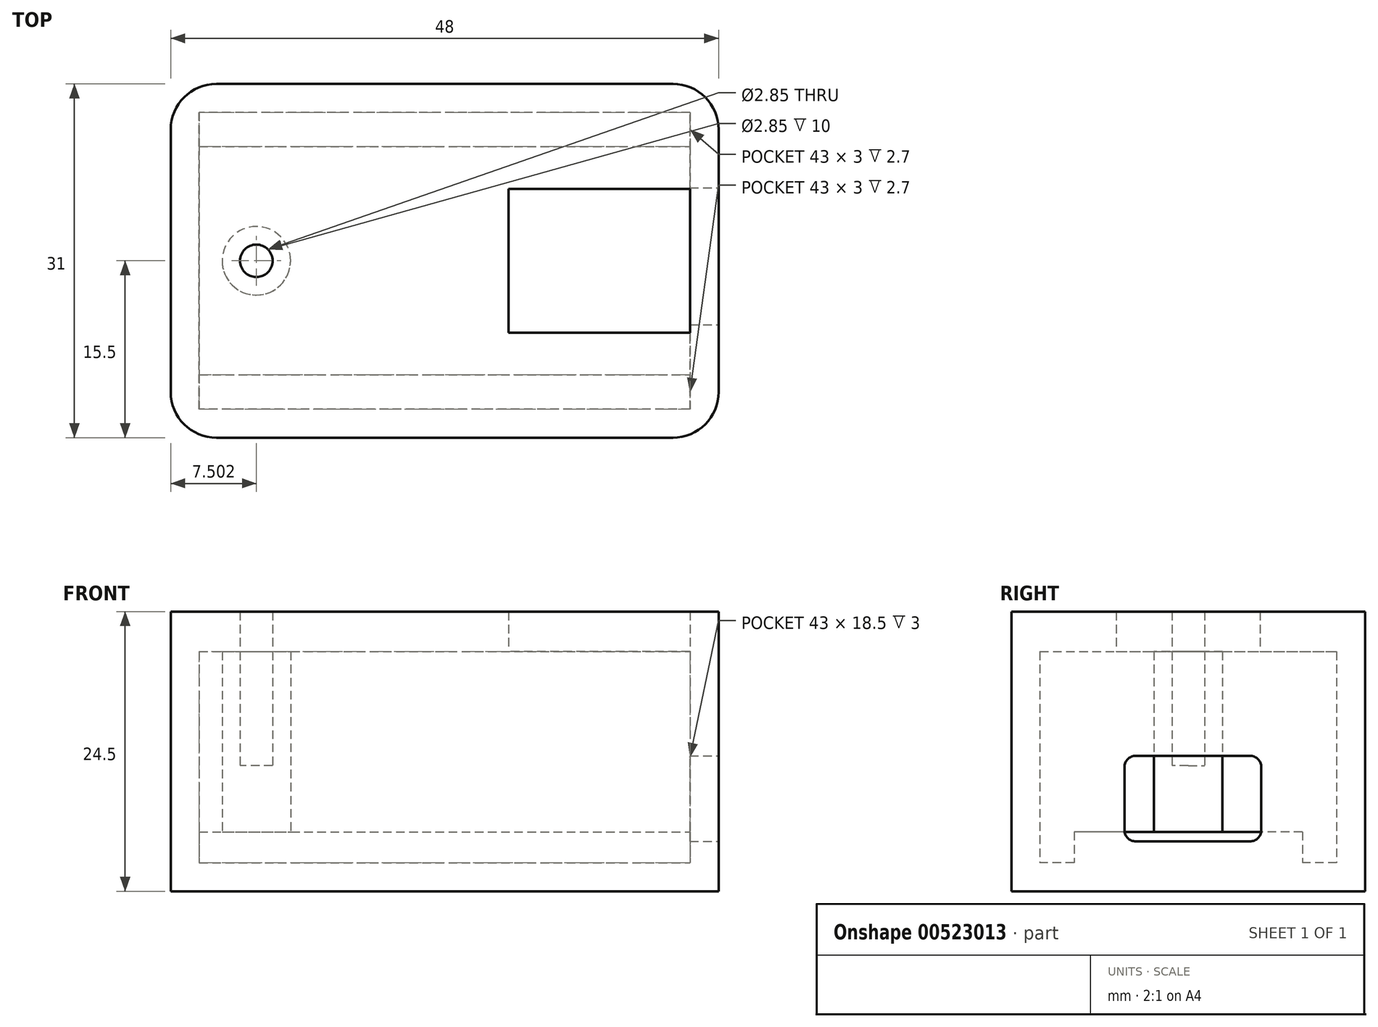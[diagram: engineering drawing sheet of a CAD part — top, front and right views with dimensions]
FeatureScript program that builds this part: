
annotation { "Feature Type Name" : "Feature", "Feature Type Description" : "" }
export const myFeature = defineFeature(function(context is Context, id is Id, definition is map)
    precondition{}
    {
        {
            var Q0;
            Q0=qCreatedBy(makeId("Top.planeOp"),FACE);
            var sketch = newSketch(context, id + "F0", { "sketchPlane" : qUnion([Q0])});
            skLineSegment(sketch, "E0.bottom", {"start": v(24, 15.5) * mm, "end": v(-24, 15.5) * mm});
            skLineSegment(sketch, "E0.top", {"start": v(24, -15.5) * mm, "end": v(-24, -15.5) * mm});
            skLineSegment(sketch, "E0.left", {"start": v(24, 15.5) * mm, "end": v(24, -15.5) * mm});
            skLineSegment(sketch, "E0.right", {"start": v(-24, 15.5) * mm, "end": v(-24, -15.5) * mm});
            skPoint(sketch, "E0.middle", {"position": v(0, 0) * mm});
            skSolve(sketch);
        }
        {
            var Q0;
            Q0=makeQuery(id+"F0.imprint","IMPRINT",FACE,{"disambiguationData":[TD([[makeQuery(id+"F0.imprint","IMPRINT",EDGE,{"derivedFrom":sQuery(id+"F0.wireOp",EDGE,"E0.bottom")}),1.0]])]});
            extrude(context, id + "F1", {"entities" : qUnion([Q0]), "depth" : 22 * mm, "offsetDistance" : 25 * mm});
        }
        {
            var Q0;
            Q0=makeQuery(id+"F1.opExtrude","CAP_FACE",FACE,{"disambiguationData":[OSD([sQuery(id+"F0.wireOp",EDGE,"E0.bottom"),sQuery(id+"F0.wireOp",EDGE,"E0.top"),sQuery(id+"F0.wireOp",EDGE,"E0.left"),sQuery(id+"F0.wireOp",EDGE,"E0.right")])],"isStart":false});
            shell(context, id + "F2", {"entities" : qUnion([Q0]), "thickness" : 2.5 * mm});
        }
        {
            var Q0;
            Q0=makeQuery(id+"F2.opShell","OFFSET_FACE",FACE,{"disambiguationData":[OSD([sQuery(id+"F0.wireOp",EDGE,"E0.bottom"),sQuery(id+"F0.wireOp",EDGE,"E0.top"),sQuery(id+"F0.wireOp",EDGE,"E0.left"),sQuery(id+"F0.wireOp",EDGE,"E0.right")])]});
            var sketch = newSketch(context, id + "F3", { "sketchPlane" : qUnion([Q0])});
            skLineSegment(sketch, "E1.bottom", {"start": v(-21.5, 10) * mm, "end": v(21.5, 10) * mm});
            skLineSegment(sketch, "E1.top", {"start": v(-21.5, -10) * mm, "end": v(21.5, -10) * mm});
            skLineSegment(sketch, "E1.left", {"start": v(-21.5, 10) * mm, "end": v(-21.5, -10) * mm});
            skLineSegment(sketch, "E1.right", {"start": v(21.5, 10) * mm, "end": v(21.5, -10) * mm});
            skPoint(sketch, "E1.middle", {"position": v(0, 0) * mm});
            skSolve(sketch);
        }
        {
            var Q0;
            Q0=makeQuery(id+"F3.imprint","IMPRINT",FACE,{"disambiguationData":[TD([[makeQuery(id+"F3.imprint","IMPRINT",EDGE,{"derivedFrom":sQuery(id+"F3.wireOp",EDGE,"E1.bottom")}),-1.0]])]});
            extrude(context, id + "F4", {"entities" : qUnion([Q0]), "operationType" : NewBodyOperationType.ADD, "depth" : 2.7 * mm, "offsetDistance" : 25 * mm});
        }
        {
            var Q0;
            Q0=makeQuery(id+"F1.opExtrude","CAP_FACE",FACE,{"disambiguationData":[OSD([sQuery(id+"F0.wireOp",EDGE,"E0.bottom"),sQuery(id+"F0.wireOp",EDGE,"E0.top"),sQuery(id+"F0.wireOp",EDGE,"E0.left"),sQuery(id+"F0.wireOp",EDGE,"E0.right")])],"isStart":false});
            cPlane(context, id + "F5", {"entities" : qUnion([Q0]), "cplaneType" : CPlaneType.OFFSET, "offset" : 2.5 * mm, "width" : 150 * mm, "height" : 150 * mm});
        }
        {
            var Q0;
            Q0=qCreatedBy(id+"F5.planeOp",FACE);
            var sketch = newSketch(context, id + "F6", { "sketchPlane" : qUnion([Q0])});
            skLineSegment(sketch, "E2.bottom", {"start": v(24, 15.5) * mm, "end": v(-24, 15.5) * mm});
            skLineSegment(sketch, "E2.top", {"start": v(24, -15.5) * mm, "end": v(-24, -15.5) * mm});
            skLineSegment(sketch, "E2.left", {"start": v(24, 15.5) * mm, "end": v(24, -15.5) * mm});
            skLineSegment(sketch, "E2.right", {"start": v(-24, 15.5) * mm, "end": v(-24, -15.5) * mm});
            skPoint(sketch, "E2.middle", {"position": v(0, 0) * mm});
            skSolve(sketch);
        }
        {
            var Q0;
            Q0=makeQuery(id+"F6.imprint","IMPRINT",FACE,{"disambiguationData":[TD([[makeQuery(id+"F6.imprint","IMPRINT",EDGE,{"derivedFrom":sQuery(id+"F6.wireOp",EDGE,"E2.bottom")}),1.0]])]});
            extrude(context, id + "F7", {"entities" : qUnion([Q0]), "oppositeDirection" : true, "depth" : 2.5 * mm, "offsetDistance" : 25 * mm});
        }
        {
            var Q0;
            Q0=makeQuery(id+"F7.opExtrude","CAP_FACE",FACE,{"disambiguationData":[OSD([sQuery(id+"F6.wireOp",EDGE,"E2.bottom"),sQuery(id+"F6.wireOp",EDGE,"E2.top"),sQuery(id+"F6.wireOp",EDGE,"E2.left"),sQuery(id+"F6.wireOp",EDGE,"E2.right")])],"isStart":false});
            var sketch = newSketch(context, id + "F8", { "sketchPlane" : qUnion([Q0])});
            skLineSegment(sketch, "E3.bottom", {"start": v(21.5, 13.05) * mm, "end": v(-21.5, 13.05) * mm});
            skLineSegment(sketch, "E3.top", {"start": v(21.5, -13.05) * mm, "end": v(-21.5, -13.05) * mm});
            skLineSegment(sketch, "E3.left", {"start": v(21.5, 13.05) * mm, "end": v(21.5, -13.05) * mm});
            skLineSegment(sketch, "E3.right", {"start": v(-21.5, 13.05) * mm, "end": v(-21.5, -13.05) * mm});
            skPoint(sketch, "E3.middle", {"position": v(0, 0) * mm});
            skSolve(sketch);
        }
        {
            var Q0;
            Q0=makeQuery(id+"F8.imprint","IMPRINT",FACE,{"disambiguationData":[TD([[makeQuery(id+"F8.imprint","IMPRINT",EDGE,{"derivedFrom":sQuery(id+"F8.wireOp",EDGE,"E3.bottom")}),1.0]])]});
            extrude(context, id + "F9", {"entities" : qUnion([Q0]), "operationType" : NewBodyOperationType.ADD, "depth" : 1 * mm, "offsetDistance" : 25 * mm});
        }
        {
            var Q0;
            Q0=makeQuery(id+"F9.opExtrude","CAP_FACE",FACE,{"disambiguationData":[OSD([sQuery(id+"F8.wireOp",EDGE,"E3.bottom"),sQuery(id+"F8.wireOp",EDGE,"E3.top"),sQuery(id+"F8.wireOp",EDGE,"E3.left"),sQuery(id+"F8.wireOp",EDGE,"E3.right")])],"isStart":false});
            var sketch = newSketch(context, id + "F10", { "sketchPlane" : qUnion([Q0])});
            skLineSegment(sketch, "E4", {"start": v(-21.5, 0) * mm, "end": v(21.5, 0) * mm, "construction": true});
            skLineSegment(sketch, "E5.bottom", {"start": v(21.5, 6.3) * mm, "end": v(5.6, 6.3) * mm});
            skLineSegment(sketch, "E5.top", {"start": v(21.5, -6.3) * mm, "end": v(5.6, -6.3) * mm});
            skLineSegment(sketch, "E5.left", {"start": v(21.5, 6.3) * mm, "end": v(21.5, -6.3) * mm});
            skLineSegment(sketch, "E5.right", {"start": v(5.6, 6.3) * mm, "end": v(5.6, -6.3) * mm});
            skSolve(sketch);
        }
        {
            var Q0;
            Q0=makeQuery(id+"F10.imprint","IMPRINT",FACE,{"disambiguationData":[TD([[makeQuery(id+"F10.imprint","IMPRINT",EDGE,{"derivedFrom":sQuery(id+"F10.wireOp",EDGE,"E5.bottom")}),1.0]])]});
            var Q1;
            Q1=makeQuery(id+"F7.opExtrude","CAP_FACE",FACE,{"disambiguationData":[OSD([sQuery(id+"F6.wireOp",EDGE,"E2.bottom"),sQuery(id+"F6.wireOp",EDGE,"E2.top"),sQuery(id+"F6.wireOp",EDGE,"E2.left"),sQuery(id+"F6.wireOp",EDGE,"E2.right")])],"isStart":true});
            extrude(context, id + "F11", {"entities" : qUnion([Q0]), "operationType" : NewBodyOperationType.REMOVE, "endBound" : BoundingType.UP_TO_SURFACE, "oppositeDirection" : true, "depth" : 25 * mm, "endBoundEntityFace" : qUnion([Q1]), "offsetDistance" : 25 * mm});
        }
        {
            var Q0;
            Q0=makeQuery(id+"F1.opExtrude","SWEPT_EDGE",EDGE,{"disambiguationData":[OSD([sQuery(id+"F0.wireOp",EDGE,"E0.top"),sQuery(id+"F0.wireOp",EDGE,"E0.left")])]});
            var Q1;
            Q1=makeQuery(id+"F1.opExtrude","SWEPT_EDGE",EDGE,{"disambiguationData":[OSD([sQuery(id+"F0.wireOp",EDGE,"E0.top"),sQuery(id+"F0.wireOp",EDGE,"E0.right")])]});
            var Q2;
            Q2=makeQuery(id+"F1.opExtrude","SWEPT_EDGE",EDGE,{"disambiguationData":[OSD([sQuery(id+"F0.wireOp",EDGE,"E0.bottom"),sQuery(id+"F0.wireOp",EDGE,"E0.right")])]});
            var Q3;
            Q3=makeQuery(id+"F1.opExtrude","SWEPT_EDGE",EDGE,{"disambiguationData":[OSD([sQuery(id+"F0.wireOp",EDGE,"E0.bottom"),sQuery(id+"F0.wireOp",EDGE,"E0.left")])]});
            var Q4;
            Q4=makeQuery(id+"F7.opExtrude","SWEPT_EDGE",EDGE,{"disambiguationData":[OSD([sQuery(id+"F6.wireOp",EDGE,"E2.top"),sQuery(id+"F6.wireOp",EDGE,"E2.left")])]});
            var Q5;
            Q5=makeQuery(id+"F7.opExtrude","SWEPT_EDGE",EDGE,{"disambiguationData":[OSD([sQuery(id+"F6.wireOp",EDGE,"E2.bottom"),sQuery(id+"F6.wireOp",EDGE,"E2.left")])]});
            var Q6;
            Q6=makeQuery(id+"F7.opExtrude","SWEPT_EDGE",EDGE,{"disambiguationData":[OSD([sQuery(id+"F6.wireOp",EDGE,"E2.top"),sQuery(id+"F6.wireOp",EDGE,"E2.right")])]});
            var Q7;
            Q7=makeQuery(id+"F7.opExtrude","SWEPT_EDGE",EDGE,{"disambiguationData":[OSD([sQuery(id+"F6.wireOp",EDGE,"E2.bottom"),sQuery(id+"F6.wireOp",EDGE,"E2.right")])]});
            fillet(context, id + "F12", {"entities" : qUnion([Q0, Q1, Q2, Q3, Q4, Q5, Q6, Q7]), "radius" : 4 * mm, "tangentPropagation" : true, "allowEdgeOverflow" : false});
        }
        {
            var Q0;
            Q0=makeQuery(id+"F1.opExtrude","SWEPT_FACE",FACE,{"disambiguationData":[OSD([sQuery(id+"F0.wireOp",EDGE,"E0.left")])]});
            var sketch = newSketch(context, id + "F13", { "sketchPlane" : qUnion([Q0])});
            skLineSegment(sketch, "E6.bottom", {"start": v(-5.6, 11.87) * mm, "end": v(6.4, 11.87) * mm});
            skLineSegment(sketch, "E6.top", {"start": v(-5.6, 4.37) * mm, "end": v(6.4, 4.37) * mm});
            skLineSegment(sketch, "E6.left", {"start": v(-5.6, 11.87) * mm, "end": v(-5.6, 4.37) * mm});
            skLineSegment(sketch, "E6.right", {"start": v(6.4, 11.87) * mm, "end": v(6.4, 4.37) * mm});
            skLineSegment(sketch, "E7", {"start": v(0.4, 0) * mm, "end": v(0.4, 22) * mm, "construction": true});
            skPoint(sketch, "E7.startSnap0", {"position": v(0.4, 11.87) * mm});
            skSolve(sketch);
        }
        {
            var Q0;
            Q0=makeQuery(id+"F13.imprint","IMPRINT",FACE,{"disambiguationData":[TD([[makeQuery(id+"F13.imprint","IMPRINT",EDGE,{"derivedFrom":sQuery(id+"F13.wireOp",EDGE,"E6.bottom")}),-1.0]])]});
            var Q1;
            Q1=makeQuery(id+"F2.opShell","OFFSET_FACE",FACE,{"disambiguationData":[OSD([sQuery(id+"F0.wireOp",EDGE,"E0.left")])]});
            extrude(context, id + "F14", {"entities" : qUnion([Q0]), "operationType" : NewBodyOperationType.REMOVE, "endBound" : BoundingType.UP_TO_SURFACE, "oppositeDirection" : true, "depth" : 25 * mm, "endBoundEntityFace" : qUnion([Q1]), "offsetDistance" : 25 * mm});
        }
        {
            var Q0;
            Q0=makeQuery(id+"F14.boolean.opBoolean","COPY",EDGE,{"derivedFrom":makeQuery(id+"F14.opExtrude","SWEPT_EDGE",EDGE,{"disambiguationData":[OSD([sQuery(id+"F13.wireOp",EDGE,"E6.top"),sQuery(id+"F13.wireOp",EDGE,"E6.left")])]})});
            var Q1;
            Q1=makeQuery(id+"F14.boolean.opBoolean","COPY",EDGE,{"derivedFrom":makeQuery(id+"F14.opExtrude","SWEPT_EDGE",EDGE,{"disambiguationData":[OSD([sQuery(id+"F13.wireOp",EDGE,"E6.top"),sQuery(id+"F13.wireOp",EDGE,"E6.right")])]})});
            var Q2;
            Q2=makeQuery(id+"F14.boolean.opBoolean","COPY",EDGE,{"derivedFrom":makeQuery(id+"F14.opExtrude","SWEPT_EDGE",EDGE,{"disambiguationData":[OSD([sQuery(id+"F13.wireOp",EDGE,"E6.bottom"),sQuery(id+"F13.wireOp",EDGE,"E6.right")])]})});
            var Q3;
            Q3=makeQuery(id+"F14.boolean.opBoolean","COPY",EDGE,{"derivedFrom":makeQuery(id+"F14.opExtrude","SWEPT_EDGE",EDGE,{"disambiguationData":[OSD([sQuery(id+"F13.wireOp",EDGE,"E6.bottom"),sQuery(id+"F13.wireOp",EDGE,"E6.left")])]})});
            fillet(context, id + "F15", {"entities" : qUnion([Q0, Q1, Q2, Q3]), "radius" : 1 * mm, "tangentPropagation" : true, "allowEdgeOverflow" : false});
        }
        {
            var Q0;
            Q0=makeQuery(id+"F4.opExtrude","CAP_FACE",FACE,{"disambiguationData":[OSD([sQuery(id+"F3.wireOp",EDGE,"E1.bottom"),sQuery(id+"F3.wireOp",EDGE,"E1.top"),sQuery(id+"F3.wireOp",EDGE,"E1.left"),sQuery(id+"F3.wireOp",EDGE,"E1.right")])],"isStart":false});
            var sketch = newSketch(context, id + "F16", { "sketchPlane" : qUnion([Q0])});
            skCircle(sketch, "E8", {"center": v(-16.5, 0) * mm, "radius": 3 * mm});
            skSolve(sketch);
        }
        {
            var Q0;
            Q0=makeQuery(id+"F16.imprint","IMPRINT",FACE,{"disambiguationData":[TD([[makeQuery(id+"F16.imprint","IMPRINT",EDGE,{"derivedFrom":sQuery(id+"F16.wireOp",EDGE,"E8")}),1.0]])]});
            var Q1;
            Q1=sQuery(id+"F16.wireOp",EDGE,"E8");
            extrude(context, id + "F17", {"entities" : qUnion([Q0]), "surfaceEntities" : qUnion([Q1]), "endBound" : BoundingType.UP_TO_NEXT, "depth" : 25 * mm, "offsetDistance" : 25 * mm});
        }
        {
            var Q0;
            Q0=makeQuery(id+"F17.opExtrude","CAP_FACE",FACE,{"disambiguationData":[OSD([sQuery(id+"F16.wireOp",EDGE,"E8")])],"isStart":false});
            var sketch = newSketch(context, id + "F18", { "sketchPlane" : qUnion([Q0])});
            skCircle(sketch, "E9", {"center": v(-16.5, 0) * mm, "radius": 1.43 * mm});
            skSolve(sketch);
        }
        {
            var Q0;
            Q0=makeQuery(id+"F18.imprint","IMPRINT",FACE,{"disambiguationData":[TD([[makeQuery(id+"F18.imprint","IMPRINT",EDGE,{"derivedFrom":sQuery(id+"F18.wireOp",EDGE,"E9")}),1.0]])]});
            var Q1;
            Q1=makeQuery(id+"F7.opExtrude","CAP_FACE",FACE,{"disambiguationData":[OSD([sQuery(id+"F6.wireOp",EDGE,"E2.bottom"),sQuery(id+"F6.wireOp",EDGE,"E2.top"),sQuery(id+"F6.wireOp",EDGE,"E2.left"),sQuery(id+"F6.wireOp",EDGE,"E2.right")])],"isStart":true});
            extrude(context, id + "F19", {"entities" : qUnion([Q0]), "operationType" : NewBodyOperationType.REMOVE, "endBound" : BoundingType.UP_TO_SURFACE, "depth" : 25 * mm, "endBoundEntityFace" : qUnion([Q1]), "offsetDistance" : 25 * mm, "hasSecondDirection" : true, "secondDirectionOppositeDirection" : true, "secondDirectionDepth" : 10 * mm});
        }
    });
